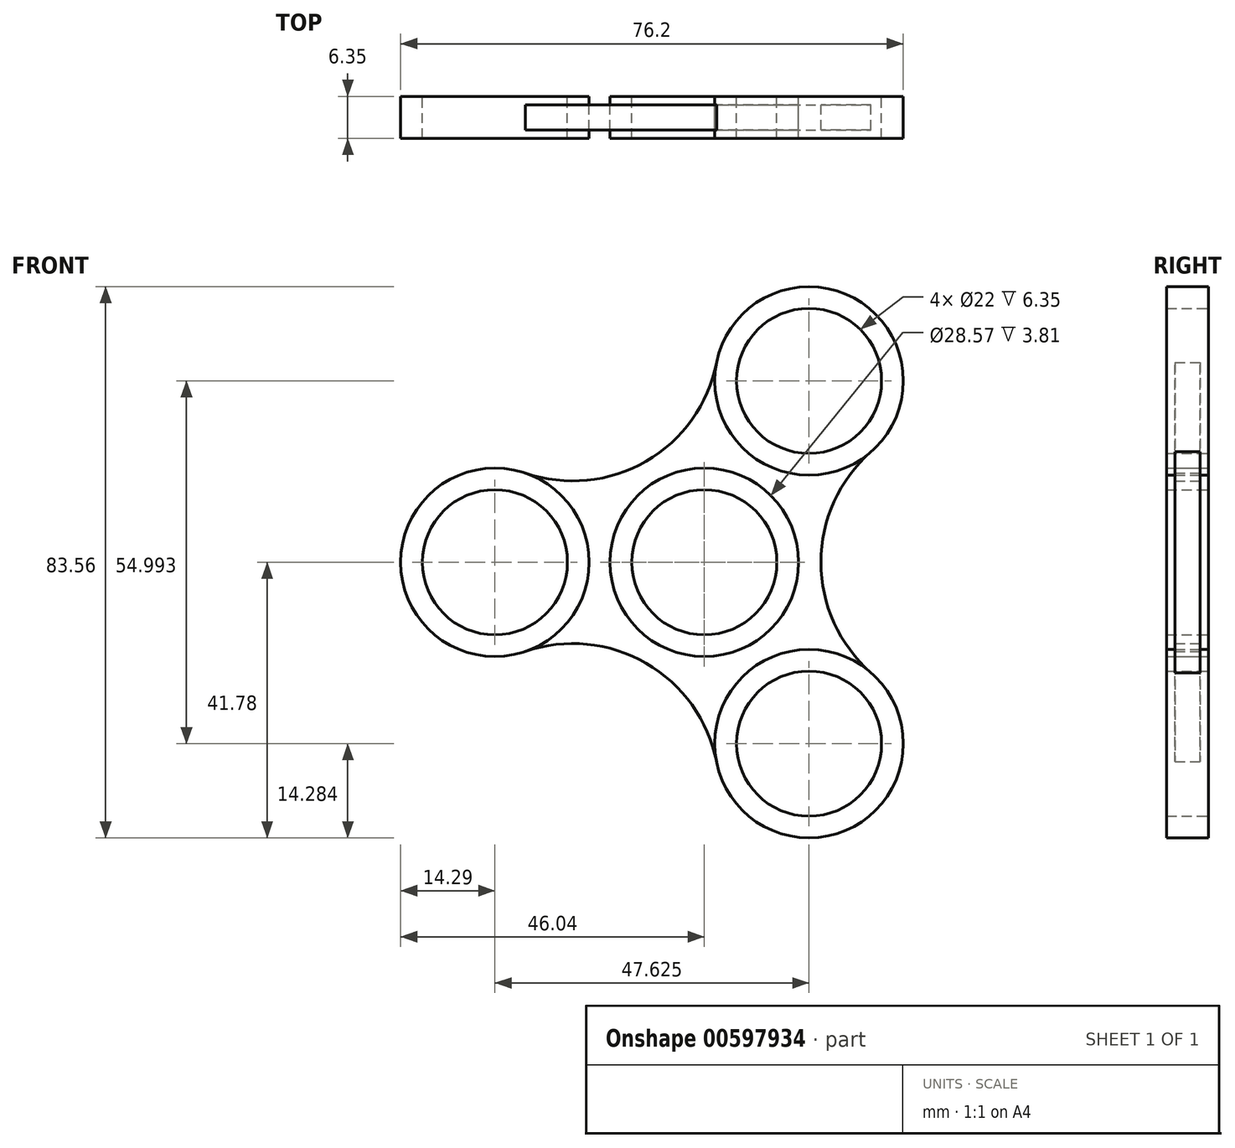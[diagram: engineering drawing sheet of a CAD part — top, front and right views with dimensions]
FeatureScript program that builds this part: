
annotation { "Feature Type Name" : "Feature", "Feature Type Description" : "" }
export const myFeature = defineFeature(function(context is Context, id is Id, definition is map)
    precondition{}
    {
        {
            var Q0;
            Q0=qCreatedBy(makeId("Front.planeOp"),FACE);
            var sketch = newSketch(context, id + "F0", { "sketchPlane" : qUnion([Q0])});
            skCircle(sketch, "E0", {"center": v(0, 0) * mm, "radius": 14.29 * mm});
            skCircle(sketch, "E1", {"center": v(0, 0) * mm, "radius": 11 * mm});
            skCircle(sketch, "E2", {"center": v(-31.75, 0) * mm, "radius": 14.29 * mm});
            skCircle(sketch, "E3", {"center": v(-31.75, 0) * mm, "radius": 11 * mm});
            skCircle(sketch, "E4.1.0", {"center": v(15.87, -27.5) * mm, "radius": 14.29 * mm});
            skCircle(sketch, "E4.1.1", {"center": v(15.87, -27.5) * mm, "radius": 11 * mm});
            skCircle(sketch, "E4.2.0", {"center": v(15.88, 27.5) * mm, "radius": 14.29 * mm});
            skCircle(sketch, "E4.2.1", {"center": v(15.88, 27.5) * mm, "radius": 11 * mm});
            skSolve(sketch);
        }
        {
            var Q0;
            Q0=qCreatedBy(makeId("Front.planeOp"),FACE);
            var sketch = newSketch(context, id + "F1", { "sketchPlane" : qUnion([Q0])});
            skArc(sketch, "E5", {"start": v(-27.13, 13.52) * mm, "mid": v(-8.84, 15.3) * mm, "end": v(1.86, 30.26) * mm});
            skArc(sketch, "E6", {"start": v(25.28, 16.74) * mm, "mid": v(17.67, 0) * mm, "end": v(25.28, -16.74) * mm});
            skArc(sketch, "E7", {"start": v(1.86, -30.26) * mm, "mid": v(-8.84, -15.3) * mm, "end": v(-27.13, -13.52) * mm});
            skCircle(sketch, "E8.0", {"center": v(15.88, 27.5) * mm, "radius": 14.29 * mm});
            skCircle(sketch, "E9.0", {"center": v(15.88, 27.5) * mm, "radius": 11 * mm});
            skCircle(sketch, "E10.0", {"center": v(0, 0) * mm, "radius": 14.29 * mm});
            skCircle(sketch, "E11.0", {"center": v(0, 0) * mm, "radius": 11 * mm});
            skCircle(sketch, "E12.0", {"center": v(15.87, -27.5) * mm, "radius": 14.29 * mm});
            skCircle(sketch, "E13.0", {"center": v(15.87, -27.5) * mm, "radius": 11 * mm});
            skCircle(sketch, "E14.0", {"center": v(-31.75, 0) * mm, "radius": 14.29 * mm});
            skCircle(sketch, "E15.0", {"center": v(-31.75, 0) * mm, "radius": 11 * mm});
            skSolve(sketch);
        }
        {
            var Q0;
            Q0=makeQuery(id+"F0.imprint","IMPRINT",FACE,{"disambiguationData":[TD([[makeQuery(id+"F0.imprint","IMPRINT",EDGE,{"derivedFrom":sQuery(id+"F0.wireOp",EDGE,"E2")}),1.0]])]});
            var Q1;
            Q1=makeQuery(id+"F0.imprint","IMPRINT",FACE,{"disambiguationData":[TD([[makeQuery(id+"F0.imprint","IMPRINT",EDGE,{"derivedFrom":sQuery(id+"F0.wireOp",EDGE,"E4.2.0")}),1.0]])]});
            var Q2;
            Q2=makeQuery(id+"F0.imprint","IMPRINT",FACE,{"disambiguationData":[TD([[makeQuery(id+"F0.imprint","IMPRINT",EDGE,{"derivedFrom":sQuery(id+"F0.wireOp",EDGE,"E4.1.0")}),1.0]])]});
            var Q3;
            Q3=makeQuery(id+"F0.imprint","IMPRINT",FACE,{"disambiguationData":[TD([[makeQuery(id+"F0.imprint","IMPRINT",EDGE,{"derivedFrom":sQuery(id+"F0.wireOp",EDGE,"E1")}),-1.0]])]});
            var Q4;
            {var subQ1=sQuery(id+"F1.wireOp",EDGE,"E5");Q4=makeQuery(id+"F1.imprint","IMPRINT",FACE,{"disambiguationData":[TD([[makeQuery(id+"F1.imprint","IMPRINT",EDGE,{"derivedFrom":subQ1}),-1.0]])]});}
            extrude(context, id + "F2", {"entities" : qUnion([Q0, Q1, Q2, Q3, Q4]), "depth" : 6.35 * mm, "offsetDistance" : 25.4 * mm});
        }
        {
            var Q0;
            Q0=makeQuery(id+"F2.opExtrude","CAP_FACE",FACE,{"disambiguationData":[OSD([sQuery(id+"F1.wireOp",EDGE,"E5"),sQuery(id+"F1.wireOp",EDGE,"E6"),sQuery(id+"F1.wireOp",EDGE,"E7"),sQuery(id+"F1.wireOp",EDGE,"E8.0"),sQuery(id+"F1.wireOp",EDGE,"E10.0"),sQuery(id+"F1.wireOp",EDGE,"E12.0"),sQuery(id+"F1.wireOp",EDGE,"E14.0")])],"isStart":true});
            extrude(context, id + "F3", {"entities" : qUnion([Q0]), "operationType" : NewBodyOperationType.REMOVE, "oppositeDirection" : true, "depth" : 1.27 * mm, "offsetDistance" : 25.4 * mm});
        }
        {
            var Q0;
            Q0=makeQuery(id+"F2.opExtrude","CAP_FACE",FACE,{"disambiguationData":[OSD([sQuery(id+"F1.wireOp",EDGE,"E5"),sQuery(id+"F1.wireOp",EDGE,"E6"),sQuery(id+"F1.wireOp",EDGE,"E7"),sQuery(id+"F1.wireOp",EDGE,"E8.0"),sQuery(id+"F1.wireOp",EDGE,"E10.0"),sQuery(id+"F1.wireOp",EDGE,"E12.0"),sQuery(id+"F1.wireOp",EDGE,"E14.0")])],"isStart":false});
            extrude(context, id + "F4", {"entities" : qUnion([Q0]), "operationType" : NewBodyOperationType.REMOVE, "oppositeDirection" : true, "depth" : 1.27 * mm, "offsetDistance" : 25.4 * mm});
        }
    });
